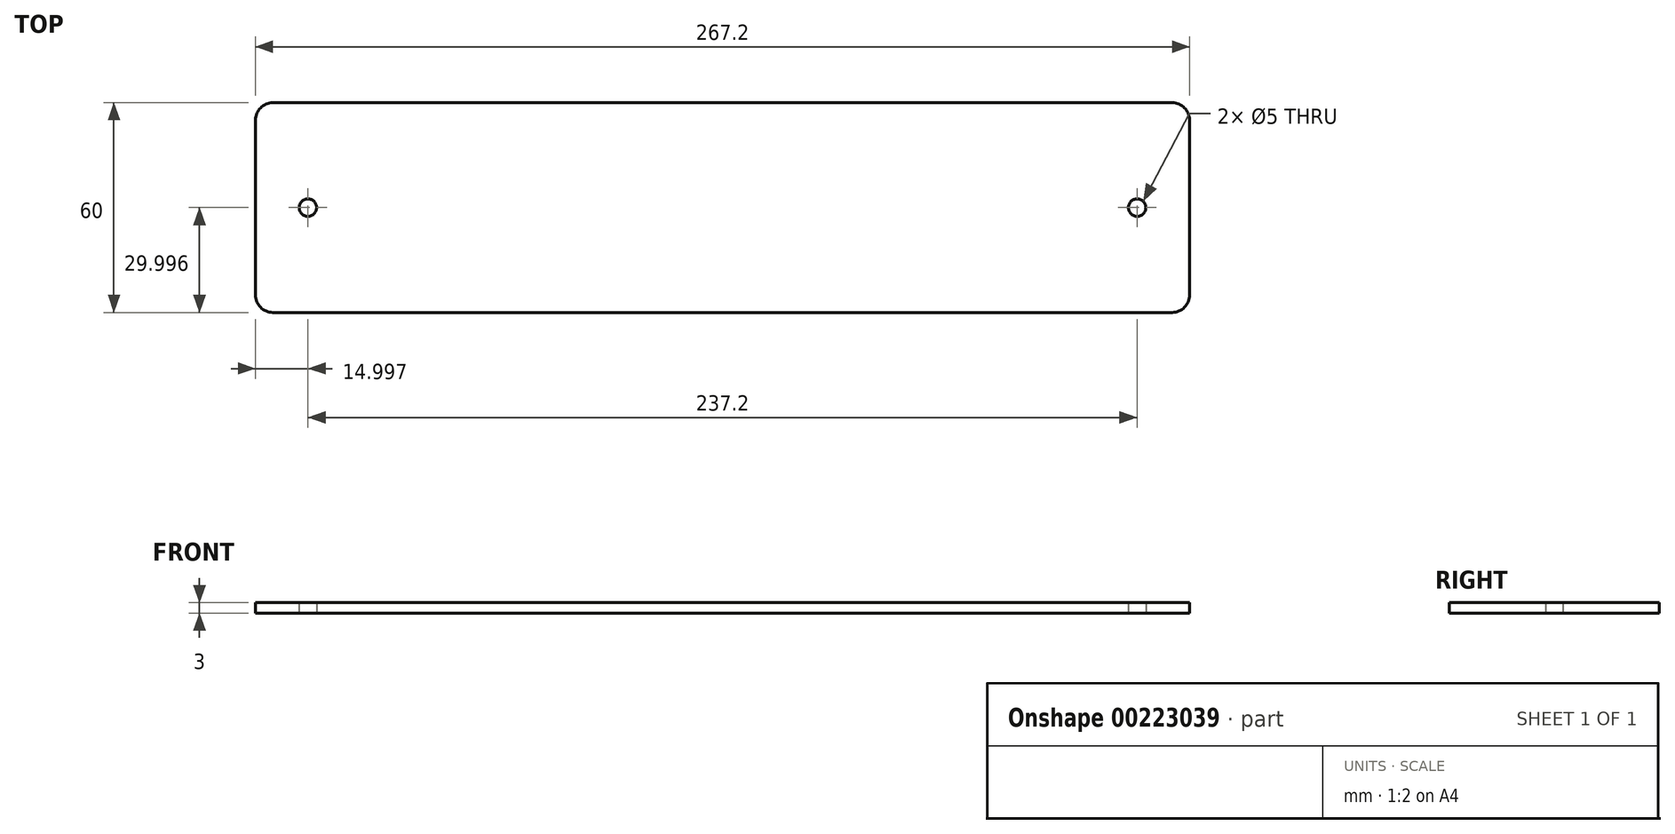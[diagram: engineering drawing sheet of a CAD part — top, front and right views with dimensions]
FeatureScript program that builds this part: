
annotation { "Feature Type Name" : "Feature", "Feature Type Description" : "" }
export const myFeature = defineFeature(function(context is Context, id is Id, definition is map)
    precondition{}
    {
        {
            var Q0;
            Q0=qCreatedBy(makeId("Top.planeOp"),FACE);
            var sketch = newSketch(context, id + "F0", { "sketchPlane" : qUnion([Q0])});
            skLineSegment(sketch, "E0", {"start": v(-117.07, -17.9) * mm, "end": v(120.13, -17.9) * mm, "construction": true});
            skLineSegment(sketch, "E1.top", {"start": v(-127.07, -47.9) * mm, "end": v(130.13, -47.9) * mm});
            skLineSegment(sketch, "E1.left", {"start": v(-132.07, 7.1) * mm, "end": v(-132.07, -42.9) * mm});
            skLineSegment(sketch, "E1.right", {"start": v(135.13, 7.1) * mm, "end": v(135.13, -42.9) * mm});
            skPoint(sketch, "E2.visualSharp", {"position": v(-132.07, 12.1) * mm});
            skArc(sketch, "E2.filletArc", {"start": v(-127.07, 12.1) * mm, "mid": v(-130.6, 10.64) * mm, "end": v(-132.07, 7.1) * mm});
            skPoint(sketch, "E3.visualSharp", {"position": v(-132.07, -47.9) * mm});
            skArc(sketch, "E3.filletArc", {"start": v(-132.07, -42.9) * mm, "mid": v(-130.6, -46.43) * mm, "end": v(-127.07, -47.9) * mm});
            skPoint(sketch, "E4.visualSharp", {"position": v(135.13, 12.1) * mm});
            skArc(sketch, "E4.filletArc", {"start": v(135.13, 7.1) * mm, "mid": v(133.66, 10.64) * mm, "end": v(130.13, 12.1) * mm});
            skPoint(sketch, "E5.visualSharp", {"position": v(135.13, -47.9) * mm});
            skArc(sketch, "E5.filletArc", {"start": v(130.13, -47.9) * mm, "mid": v(133.66, -46.43) * mm, "end": v(135.13, -42.9) * mm});
            skCircle(sketch, "E6", {"center": v(-117.07, -17.9) * mm, "radius": 2.5 * mm});
            skCircle(sketch, "E7", {"center": v(120.13, -17.9) * mm, "radius": 2.5 * mm});
            skLineSegment(sketch, "E8", {"start": v(-127.07, 12.1) * mm, "end": v(130.13, 12.1) * mm});
            skSolve(sketch);
        }
        {
            var Q0;
            Q0 = qSketchRegion(id + "F0", true);
            extrude(context, id + "F1", {"entities" : qUnion([Q0]), "depth" : 3 * mm});
        }
    });
